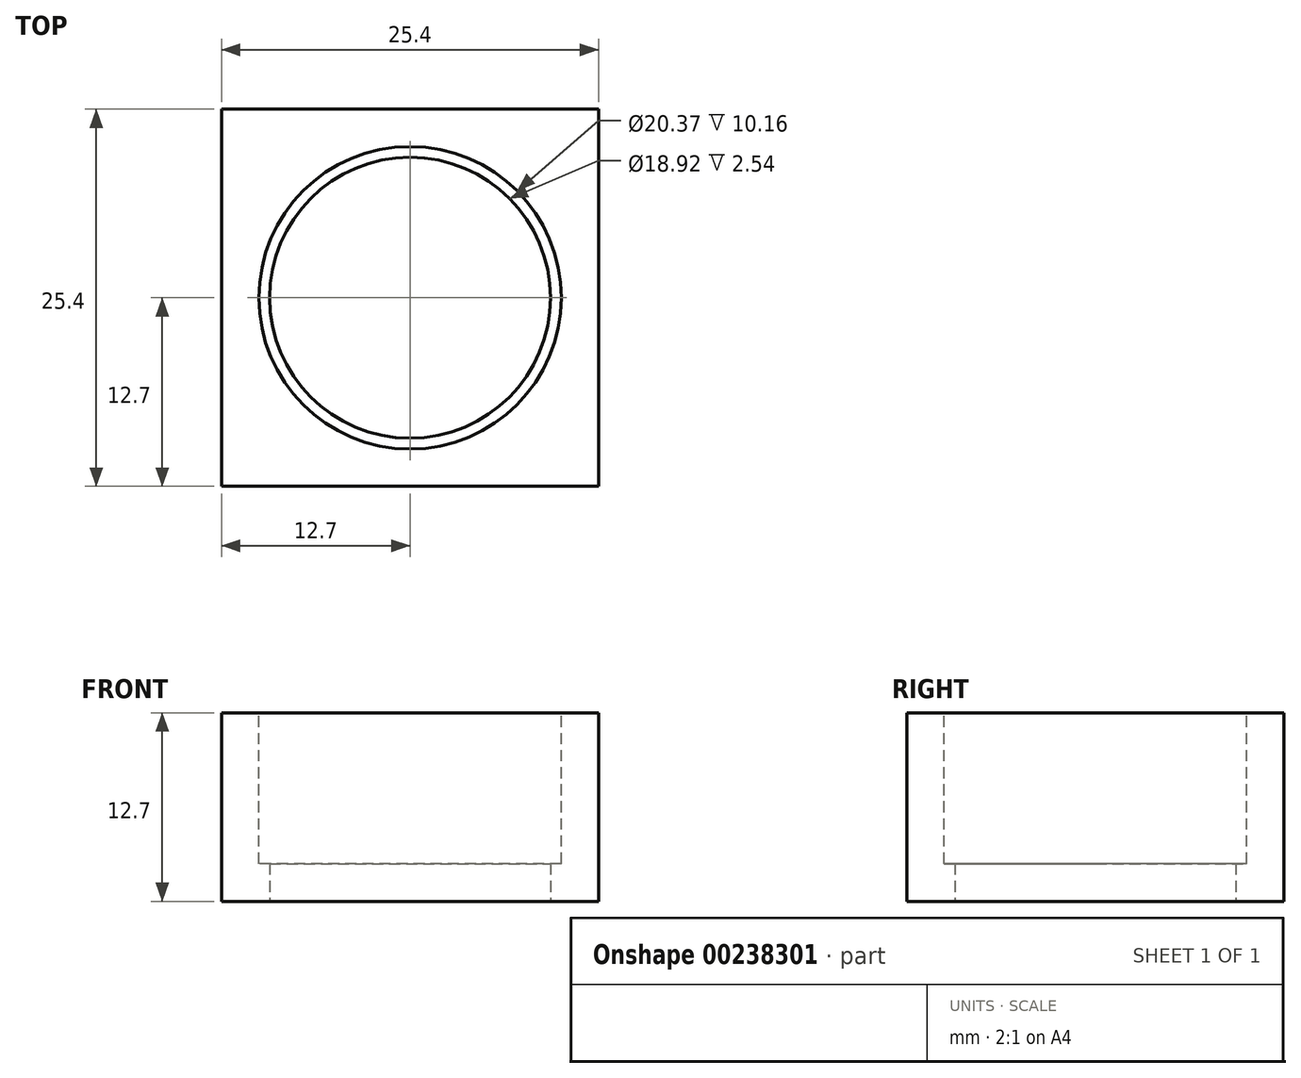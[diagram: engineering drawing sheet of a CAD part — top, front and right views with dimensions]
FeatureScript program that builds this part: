
annotation { "Feature Type Name" : "Feature", "Feature Type Description" : "" }
export const myFeature = defineFeature(function(context is Context, id is Id, definition is map)
    precondition{}
    {
        {
            var Q0;
            Q0=qCreatedBy(makeId("Top.planeOp"),FACE);
            var sketch = newSketch(context, id + "F0", { "sketchPlane" : qUnion([Q0])});
            skLineSegment(sketch, "E0.bottom", {"start": v(0, 0) * mm, "end": v(25.4, 0) * mm});
            skLineSegment(sketch, "E0.top", {"start": v(0, -25.4) * mm, "end": v(25.4, -25.4) * mm});
            skLineSegment(sketch, "E0.left", {"start": v(0, 0) * mm, "end": v(0, -25.4) * mm});
            skLineSegment(sketch, "E0.right", {"start": v(25.4, 0) * mm, "end": v(25.4, -25.4) * mm});
            skSolve(sketch);
        }
        {
            var Q0;
            Q0=makeQuery(id+"F0.imprint","IMPRINT",FACE,{"disambiguationData":[TD([[makeQuery(id+"F0.imprint","IMPRINT",EDGE,{"derivedFrom":sQuery(id+"F0.wireOp",EDGE,"E0.bottom")}),-1.0]])]});
            extrude(context, id + "F1", {"entities" : qUnion([Q0]), "depth" : 12.7 * mm});
        }
        {
            var Q0;
            Q0=makeQuery(id+"F1.opExtrude","CAP_FACE",FACE,{"disambiguationData":[OSD([sQuery(id+"F0.wireOp",EDGE,"E0.bottom"),sQuery(id+"F0.wireOp",EDGE,"E0.top"),sQuery(id+"F0.wireOp",EDGE,"E0.left"),sQuery(id+"F0.wireOp",EDGE,"E0.right")])],"isStart":false});
            var sketch = newSketch(context, id + "F2", { "sketchPlane" : qUnion([Q0])});
            skCircle(sketch, "E1", {"center": v(12.7, -12.7) * mm, "radius": 10.19 * mm});
            skSolve(sketch);
        }
        {
            var Q0;
            Q0=makeQuery(id+"F2.imprint","IMPRINT",FACE,{"disambiguationData":[TD([[makeQuery(id+"F2.imprint","IMPRINT",EDGE,{"derivedFrom":sQuery(id+"F2.wireOp",EDGE,"E1")}),1.0]])]});
            extrude(context, id + "F3", {"entities" : qUnion([Q0]), "operationType" : NewBodyOperationType.REMOVE, "oppositeDirection" : true, "depth" : 10.16 * mm});
        }
        {
            var Q0;
            Q0=makeQuery(id+"F1.opExtrude","CAP_FACE",FACE,{"disambiguationData":[OSD([sQuery(id+"F0.wireOp",EDGE,"E0.bottom"),sQuery(id+"F0.wireOp",EDGE,"E0.top"),sQuery(id+"F0.wireOp",EDGE,"E0.left"),sQuery(id+"F0.wireOp",EDGE,"E0.right")])],"isStart":true});
            var sketch = newSketch(context, id + "F4", { "sketchPlane" : qUnion([Q0])});
            skCircle(sketch, "E2", {"center": v(12.7, 12.7) * mm, "radius": 9.46 * mm});
            skSolve(sketch);
        }
        {
            var Q0;
            Q0=makeQuery(id+"F4.imprint","IMPRINT",FACE,{"disambiguationData":[TD([[makeQuery(id+"F4.imprint","IMPRINT",EDGE,{"derivedFrom":sQuery(id+"F4.wireOp",EDGE,"E2")}),1.0]])]});
            var Q1;
            Q1 = qSketchRegion(id + "F4", true);
            extrude(context, id + "F5", {"entities" : qUnion([Q0, Q1]), "operationType" : NewBodyOperationType.REMOVE, "oppositeDirection" : true, "depth" : 2.54 * mm});
        }
    });
